# Revit family: NORFAC_WENT2000 fastkarm
name_source: partatom
category: Windows
revit_build: Autodesk Revit 2018 (Build: 20170525_2315(x64)
units: mm (PartAtom-declared; Revit-internal decimal feet)

## family parameters
Always vertical = Yes
Cut with Voids When Loaded = No
Host = Wall
OmniClass Number = 23.30.20.00
OmniClass Title = Windows
Room Calculation Point = No
Shared = No

## types (1)
- TS-1-1 2
    Analytic Construction = <None>
    Case/Transom = RAL 9010
    Default Sill Height = 800 mm  [stored 2.62467 ft]
    Eref Energi balance = 3.405502
    Ew nord = -47.165967
    Ew syd = 46.726684
    Ew vest = -10.516526
    Ew øst = -10.516526
    Frame Area = 0.17 m²
    Frame Depth = 140 mm  [stored 0.459318 ft]
    Frame Width = 55 mm  [stored 0.180446 ft]
    Frame/Mullion = Softwood, Lumber
    Glass Area = 0.51 m²
    Glass Height = 570 mm
    Glass Material = BA - (o) - Glas
    Glass Width = 890 mm
    Height = 680 mm  [stored 2.23097 ft]
    Horiz Mullion 1 of 1 = No
    Horiz Mullion 1 of 2 = No
    Horiz Mullion 2 of 2 = No
    Joint = 10 mm  [stored 0.0328084 ft]
    Joint Material = Black Rubber
    LT value = 1
    Left Hinging = No
    Manual Height = 523 mm  [stored 1.71588 ft]
    Manual Width = 1020 mm  [stored 3.34646 ft]
    Placement In Wall = 0 mm  [stored 0 ft]
    Psi Glass = 0.04
    Right Hinging = No
    Rough Height = 700 mm  [stored 2.29659 ft]
    Rough Width = 1020 mm  [stored 3.34646 ft]
    Top Hinging = No
    U value = 0.854146
    U value Frame = 0.66
    U value Glass = 0.69
    Ventil mål mm = 689.5
    Ventilations luftmængde 10Pa, m3/t = 23.6
    Ventilations luftsmængde 4Pa, m3/t = 14.9
    Ventilations luftsmængde 8Pa, m3/t = 20.9
    Vinkel fra Nord = 270.00°
    Wall Closure = By host
    Width = 1000 mm  [stored 3.28084 ft]
    Window Area = 0.68 m²
    g value = 0.55
    gw = 0.410316

note: [stored X ft] marks values corroborated as IEEE doubles in the binary element streams (Revit-internal decimal feet)

## geometry (parser evidence)
native form markers: Sweep x9
no freeform markers — native parametric forms only
